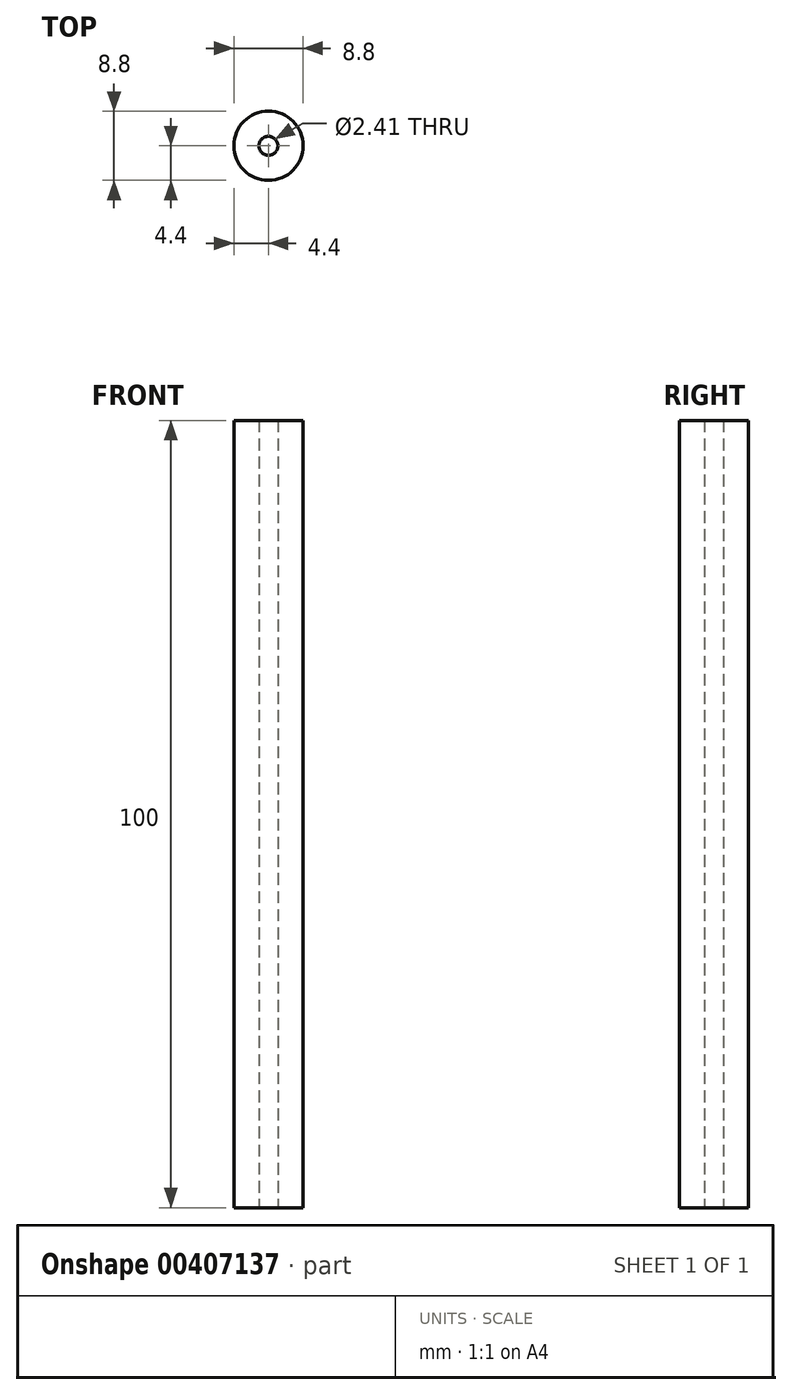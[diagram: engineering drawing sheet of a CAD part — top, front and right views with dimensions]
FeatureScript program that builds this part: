
annotation { "Feature Type Name" : "Feature", "Feature Type Description" : "" }
export const myFeature = defineFeature(function(context is Context, id is Id, definition is map)
    precondition{}
    {
        {
            var Q0;
            Q0=qCreatedBy(makeId("Top.planeOp"),FACE);
            var sketch = newSketch(context, id + "F0", { "sketchPlane" : qUnion([Q0])});
            skCircle(sketch, "E0", {"center": v(0, 0) * mm, "radius": 4.4 * mm});
            skCircle(sketch, "E1", {"center": v(0, 0) * mm, "radius": 1.2 * mm});
            skSolve(sketch);
        }
        {
            var Q0;
            Q0=qSketchRegion(id+"F0",true);
            extrude(context, id + "F1", {"entities" : qUnion([Q0]), "depth" : 100 * mm});
        }
    });
